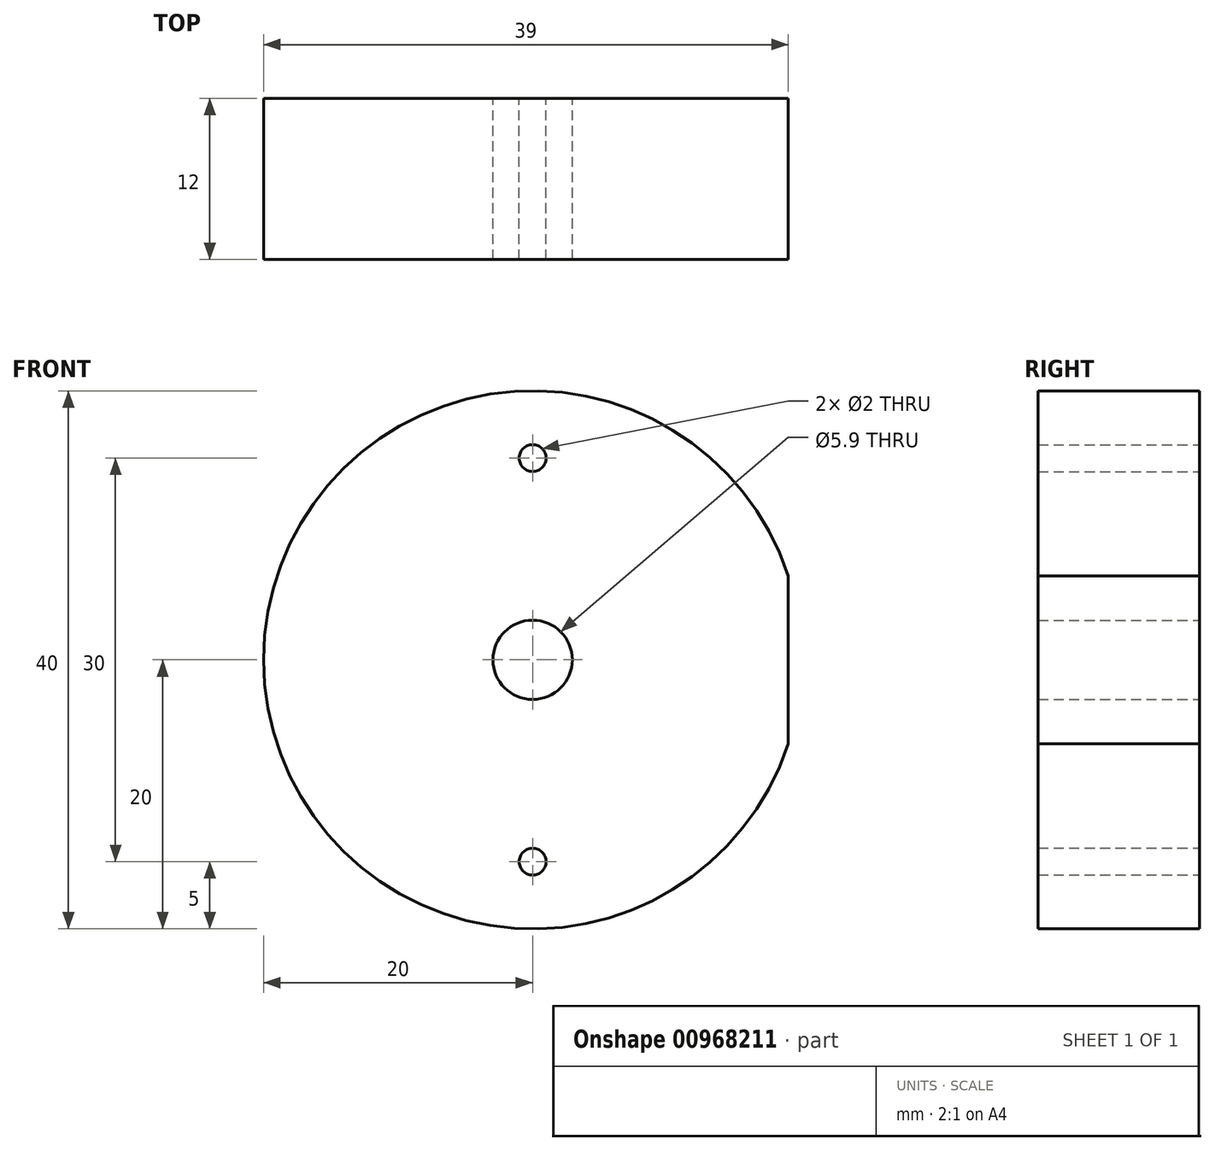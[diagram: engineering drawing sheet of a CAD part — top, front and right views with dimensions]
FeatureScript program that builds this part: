
annotation { "Feature Type Name" : "Feature", "Feature Type Description" : "" }
export const myFeature = defineFeature(function(context is Context, id is Id, definition is map)
    precondition{}
    {
        {
            var Q0;
            Q0=qCreatedBy(makeId("Front.planeOp"),FACE);
            var sketch = newSketch(context, id + "F0", { "sketchPlane" : qUnion([Q0])});
            skArc(sketch, "E0", {"start": v(19, 6.24) * mm, "mid": v(-20, 0) * mm, "end": v(19, -6.24) * mm});
            skCircle(sketch, "E1", {"center": v(0, 0) * mm, "radius": 2.95 * mm});
            skCircle(sketch, "E2", {"center": v(0, 15) * mm, "radius": 1 * mm});
            skCircle(sketch, "E3", {"center": v(0, -15) * mm, "radius": 1 * mm});
            skLineSegment(sketch, "E4", {"start": v(19, 6.24) * mm, "end": v(19, -6.24) * mm});
            skSolve(sketch);
        }
        {
            var Q0;
            Q0=makeQuery(id+"F0.imprint","IMPRINT",FACE,{"disambiguationData":[TD([[makeQuery(id+"F0.imprint","IMPRINT",EDGE,{"derivedFrom":sQuery(id+"F0.wireOp",EDGE,"E0")}),1.0]])]});
            extrude(context, id + "F1", {"entities" : qUnion([Q0]), "endBound" : BoundingType.SYMMETRIC, "depth" : 12 * mm, "offsetDistance" : 25 * mm});
        }
    });
